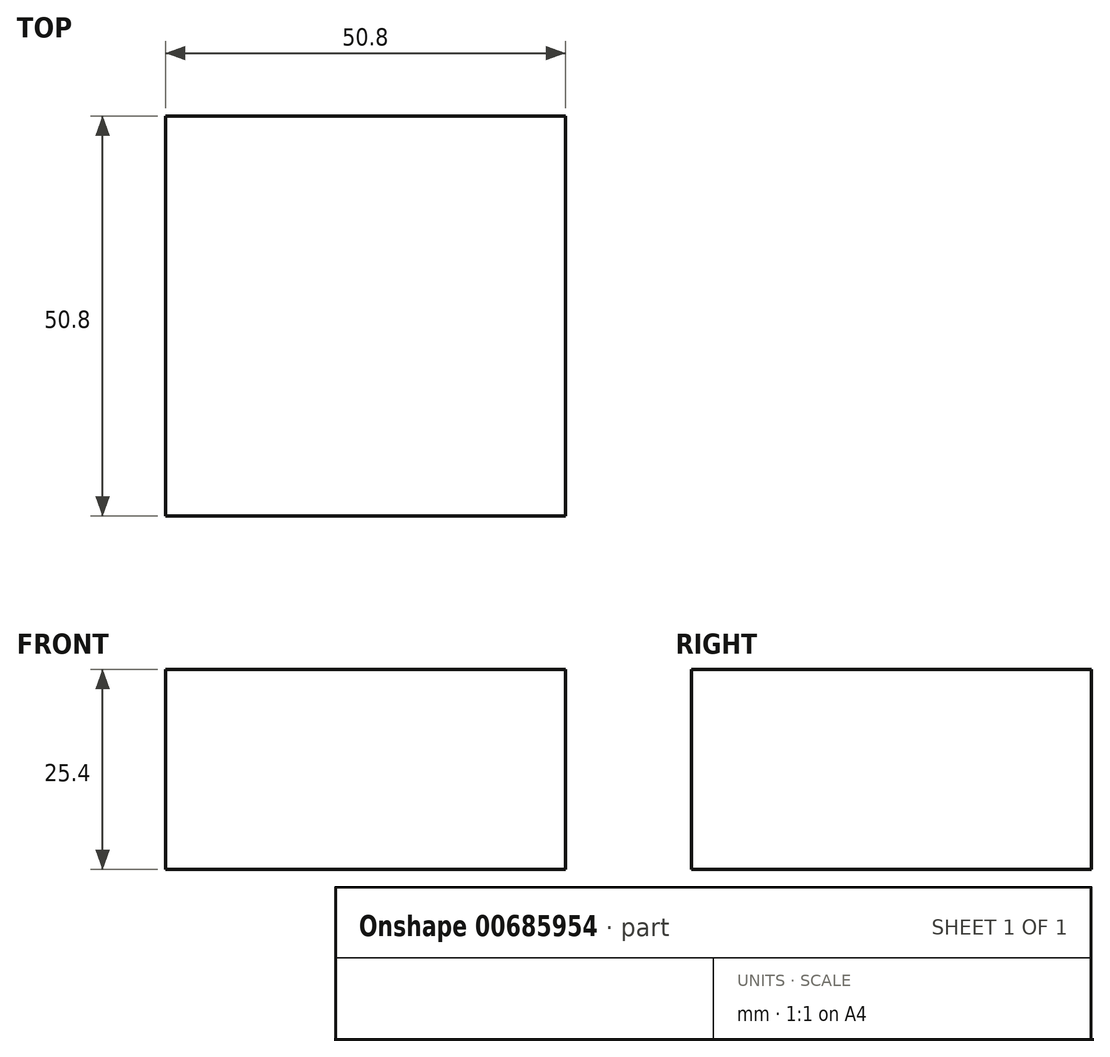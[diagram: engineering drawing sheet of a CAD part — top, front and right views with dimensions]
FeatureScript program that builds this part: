
annotation { "Feature Type Name" : "Feature", "Feature Type Description" : "" }
export const myFeature = defineFeature(function(context is Context, id is Id, definition is map)
    precondition{}
    {
        {
            var Q0;
            Q0=qCreatedBy(makeId("Top.planeOp"),FACE);
            var sketch = newSketch(context, id + "F0", { "sketchPlane" : qUnion([Q0])});
            skLineSegment(sketch, "E0.bottom", {"start": v(-27.03, 34.28) * mm, "end": v(23.77, 34.28) * mm});
            skLineSegment(sketch, "E0.top", {"start": v(-27.03, -16.52) * mm, "end": v(23.77, -16.52) * mm});
            skLineSegment(sketch, "E0.left", {"start": v(-27.03, 34.28) * mm, "end": v(-27.03, -16.52) * mm});
            skLineSegment(sketch, "E0.right", {"start": v(23.77, 34.28) * mm, "end": v(23.77, -16.52) * mm});
            skSolve(sketch);
        }
        {
            var Q0;
            Q0 = qSketchRegion(id + "F0", true);
            extrude(context, id + "F1", {"entities" : qUnion([Q0]), "depth" : 25.4 * mm, "offsetDistance" : 25.4 * mm});
        }
    });
